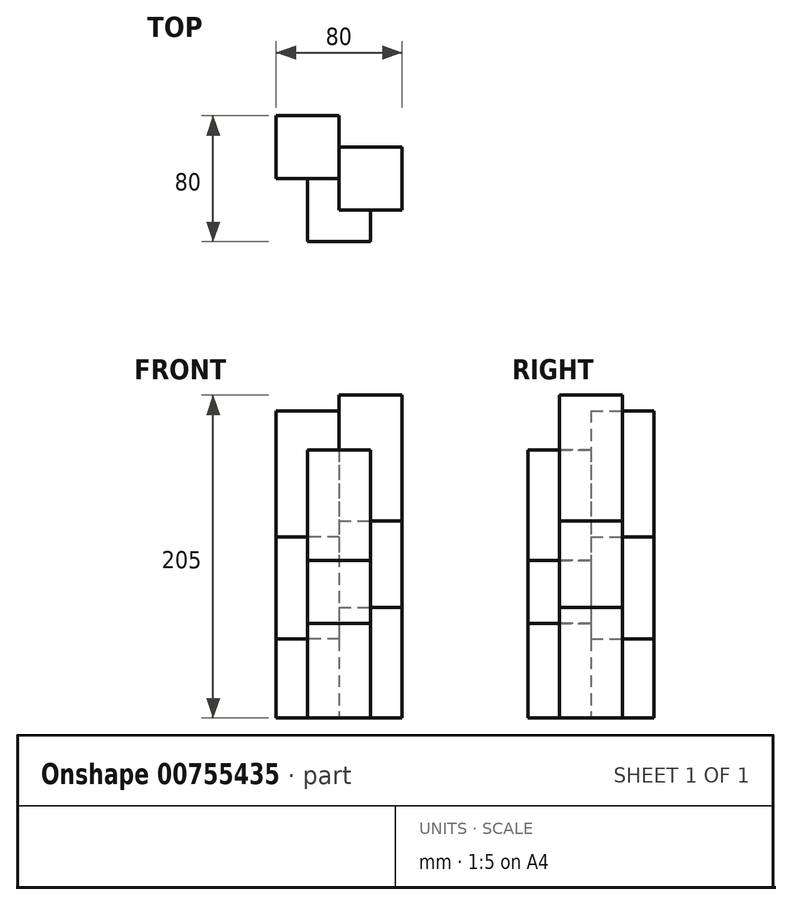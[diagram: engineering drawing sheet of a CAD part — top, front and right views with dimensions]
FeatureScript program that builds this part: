
annotation { "Feature Type Name" : "Feature", "Feature Type Description" : "" }
export const myFeature = defineFeature(function(context is Context, id is Id, definition is map)
    precondition{}
    {
        {
            var Q0;
            Q0=qCreatedBy(makeId("Top.planeOp"),FACE);
            var sketch = newSketch(context, id + "F0", { "sketchPlane" : qUnion([Q0])});
            skLineSegment(sketch, "E0.bottom", {"start": v(0, 0) * mm, "end": v(-40, 0) * mm});
            skLineSegment(sketch, "E0.top", {"start": v(0, 40) * mm, "end": v(-40, 40) * mm});
            skLineSegment(sketch, "E0.left", {"start": v(0, 0) * mm, "end": v(0, 40) * mm});
            skLineSegment(sketch, "E0.right", {"start": v(-40, 0) * mm, "end": v(-40, 40) * mm});
            skSolve(sketch);
        }
        {
            var Q0;
            Q0=makeQuery(id+"F0.imprint","IMPRINT",FACE,{"disambiguationData":[TD([[makeQuery(id+"F0.imprint","IMPRINT",EDGE,{"derivedFrom":sQuery(id+"F0.wireOp",EDGE,"E0.bottom")}),-1.0]])]});
            extrude(context, id + "F1", {"entities" : qUnion([Q0]), "depth" : 50 * mm, "offsetDistance" : 25 * mm});
        }
        {
            var Q0;
            Q0=qCreatedBy(makeId("Top.planeOp"),FACE);
            var sketch = newSketch(context, id + "F2", { "sketchPlane" : qUnion([Q0])});
            skLineSegment(sketch, "E1.bottom", {"start": v(-20, 0) * mm, "end": v(20, 0) * mm});
            skLineSegment(sketch, "E1.top", {"start": v(-20, -40) * mm, "end": v(20, -40) * mm});
            skLineSegment(sketch, "E1.left", {"start": v(-20, 0) * mm, "end": v(-20, -40) * mm});
            skLineSegment(sketch, "E1.right", {"start": v(20, 0) * mm, "end": v(20, -40) * mm});
            skSolve(sketch);
        }
        {
            var Q0;
            Q0 = qSketchRegion(id + "F2", true);
            extrude(context, id + "F3", {"entities" : qUnion([Q0]), "operationType" : NewBodyOperationType.ADD, "depth" : 60 * mm, "offsetDistance" : 25 * mm});
        }
        {
            var Q0;
            Q0=qCreatedBy(makeId("Top.planeOp"),FACE);
            var sketch = newSketch(context, id + "F4", { "sketchPlane" : qUnion([Q0])});
            skLineSegment(sketch, "E2.bottom", {"start": v(0, 20) * mm, "end": v(40, 20) * mm});
            skLineSegment(sketch, "E2.top", {"start": v(0, -20) * mm, "end": v(40, -20) * mm});
            skLineSegment(sketch, "E2.left", {"start": v(0, 20) * mm, "end": v(0, -20) * mm});
            skLineSegment(sketch, "E2.right", {"start": v(40, 20) * mm, "end": v(40, -20) * mm});
            skSolve(sketch);
        }
        {
            var Q0;
            Q0 = qSketchRegion(id + "F4", true);
            extrude(context, id + "F5", {"entities" : qUnion([Q0]), "operationType" : NewBodyOperationType.ADD, "depth" : 70 * mm, "offsetDistance" : 25 * mm});
        }
        {
            var Q0;
            Q0=makeQuery(id+"F1.opExtrude","CAP_FACE",FACE,{"disambiguationData":[OSD([sQuery(id+"F0.wireOp",EDGE,"E0.bottom"),sQuery(id+"F0.wireOp",EDGE,"E0.top"),sQuery(id+"F0.wireOp",EDGE,"E0.left"),sQuery(id+"F0.wireOp",EDGE,"E0.right")])],"isStart":false});
            var sketch = newSketch(context, id + "F6", { "sketchPlane" : qUnion([Q0])});
            skLineSegment(sketch, "E3.0.0", {"start": v(0, 0) * mm, "end": v(0, 20) * mm});
            skLineSegment(sketch, "E3.0.1", {"start": v(0, 20) * mm, "end": v(0, 40) * mm});
            skLineSegment(sketch, "E3.0.2", {"start": v(0, 40) * mm, "end": v(-40, 40) * mm});
            skLineSegment(sketch, "E3.0.3", {"start": v(-40, 40) * mm, "end": v(-40, 0) * mm});
            skLineSegment(sketch, "E3.0.4", {"start": v(-40, 0) * mm, "end": v(-20, 0) * mm});
            skLineSegment(sketch, "E3.0.5", {"start": v(-20, 0) * mm, "end": v(0, 0) * mm});
            skSolve(sketch);
        }
        {
            var Q0;
            Q0 = qSketchRegion(id + "F6", true);
            extrude(context, id + "F7", {"entities" : qUnion([Q0]), "depth" : 65 * mm, "offsetDistance" : 25 * mm});
        }
        {
            var Q0;
            Q0=makeQuery(id+"F3.opExtrude","CAP_FACE",FACE,{"disambiguationData":[OSD([sQuery(id+"F2.wireOp",EDGE,"E1.bottom"),sQuery(id+"F2.wireOp",EDGE,"E1.top"),sQuery(id+"F2.wireOp",EDGE,"E1.left"),sQuery(id+"F2.wireOp",EDGE,"E1.right")])],"isStart":false});
            var sketch = newSketch(context, id + "F8", { "sketchPlane" : qUnion([Q0])});
            skLineSegment(sketch, "E4.0.0", {"start": v(20, -20) * mm, "end": v(0, -20) * mm});
            skLineSegment(sketch, "E4.0.1", {"start": v(0, -20) * mm, "end": v(0, 0) * mm});
            skLineSegment(sketch, "E4.0.2", {"start": v(0, 0) * mm, "end": v(-20, 0) * mm});
            skLineSegment(sketch, "E4.0.3", {"start": v(-20, 0) * mm, "end": v(-20, -40) * mm});
            skLineSegment(sketch, "E4.0.4", {"start": v(-20, -40) * mm, "end": v(20, -40) * mm});
            skLineSegment(sketch, "E4.0.5", {"start": v(20, -40) * mm, "end": v(20, -20) * mm});
            skSolve(sketch);
        }
        {
            var Q0;
            Q0 = qSketchRegion(id + "F8", true);
            extrude(context, id + "F9", {"entities" : qUnion([Q0]), "depth" : 40 * mm, "offsetDistance" : 25 * mm});
        }
        {
            var Q0;
            Q0=makeQuery(id+"F5.opExtrude","CAP_FACE",FACE,{"disambiguationData":[OSD([sQuery(id+"F4.wireOp",EDGE,"E2.bottom"),sQuery(id+"F4.wireOp",EDGE,"E2.top"),sQuery(id+"F4.wireOp",EDGE,"E2.left"),sQuery(id+"F4.wireOp",EDGE,"E2.right")])],"isStart":false});
            var sketch = newSketch(context, id + "F10", { "sketchPlane" : qUnion([Q0])});
            skLineSegment(sketch, "E5.0.0", {"start": v(0, 20) * mm, "end": v(0, -20) * mm});
            skLineSegment(sketch, "E5.0.1", {"start": v(0, -20) * mm, "end": v(40, -20) * mm});
            skLineSegment(sketch, "E5.0.2", {"start": v(40, -20) * mm, "end": v(40, 20) * mm});
            skLineSegment(sketch, "E5.0.3", {"start": v(40, 20) * mm, "end": v(0, 20) * mm});
            skSolve(sketch);
        }
        {
            var Q0;
            Q0 = qSketchRegion(id + "F10", true);
            extrude(context, id + "F11", {"entities" : qUnion([Q0]), "depth" : 55 * mm, "offsetDistance" : 25 * mm});
        }
        {
            var Q0;
            Q0=makeQuery(id+"F7.opExtrude","SWEPT_BODY",BODY,{"disambiguationData":[OSD([sQuery(id+"F6.wireOp",EDGE,"E3.0.0"),sQuery(id+"F6.wireOp",EDGE,"E3.0.1"),sQuery(id+"F6.wireOp",EDGE,"E3.0.2"),sQuery(id+"F6.wireOp",EDGE,"E3.0.3"),sQuery(id+"F6.wireOp",EDGE,"E3.0.4"),sQuery(id+"F6.wireOp",EDGE,"E3.0.5")])]});
            var Q1;
            Q1=makeQuery(id+"F9.opExtrude","SWEPT_BODY",BODY,{"disambiguationData":[OSD([sQuery(id+"F8.wireOp",EDGE,"E4.0.0"),sQuery(id+"F8.wireOp",EDGE,"E4.0.1"),sQuery(id+"F8.wireOp",EDGE,"E4.0.2"),sQuery(id+"F8.wireOp",EDGE,"E4.0.3"),sQuery(id+"F8.wireOp",EDGE,"E4.0.4"),sQuery(id+"F8.wireOp",EDGE,"E4.0.5")])]});
            var Q2;
            Q2=makeQuery(id+"F11.opExtrude","SWEPT_BODY",BODY,{"disambiguationData":[OSD([sQuery(id+"F10.wireOp",EDGE,"E5.0.0"),sQuery(id+"F10.wireOp",EDGE,"E5.0.1"),sQuery(id+"F10.wireOp",EDGE,"E5.0.2"),sQuery(id+"F10.wireOp",EDGE,"E5.0.3")])]});
            booleanBodies(context, id + "F12", {"operationType" : BooleanOperationType.UNION, "tools" : qUnion([Q0, Q1, Q2])});
        }
        {
            var Q0;
            Q0=makeQuery(id+"F9.opExtrude","CAP_FACE",FACE,{"disambiguationData":[OSD([sQuery(id+"F8.wireOp",EDGE,"E4.0.0"),sQuery(id+"F8.wireOp",EDGE,"E4.0.1"),sQuery(id+"F8.wireOp",EDGE,"E4.0.2"),sQuery(id+"F8.wireOp",EDGE,"E4.0.3"),sQuery(id+"F8.wireOp",EDGE,"E4.0.4"),sQuery(id+"F8.wireOp",EDGE,"E4.0.5")])],"isStart":false});
            var sketch = newSketch(context, id + "F13", { "sketchPlane" : qUnion([Q0])});
            skLineSegment(sketch, "E6.0.0", {"start": v(20, -40) * mm, "end": v(20, -20) * mm});
            skLineSegment(sketch, "E6.0.1", {"start": v(20, -20) * mm, "end": v(0, -20) * mm});
            skLineSegment(sketch, "E6.0.2", {"start": v(0, -20) * mm, "end": v(0, 0) * mm});
            skLineSegment(sketch, "E6.0.3", {"start": v(0, 0) * mm, "end": v(-20, 0) * mm});
            skLineSegment(sketch, "E6.0.4", {"start": v(-20, 0) * mm, "end": v(-20, -40) * mm});
            skLineSegment(sketch, "E6.0.5", {"start": v(-20, -40) * mm, "end": v(20, -40) * mm});
            skSolve(sketch);
        }
        {
            var Q0;
            Q0 = qSketchRegion(id + "F13", true);
            extrude(context, id + "F14", {"entities" : qUnion([Q0]), "depth" : 70 * mm, "offsetDistance" : 25 * mm});
        }
        {
            var Q0;
            Q0=makeQuery(id+"F7.opExtrude","CAP_FACE",FACE,{"disambiguationData":[OSD([sQuery(id+"F6.wireOp",EDGE,"E3.0.0"),sQuery(id+"F6.wireOp",EDGE,"E3.0.1"),sQuery(id+"F6.wireOp",EDGE,"E3.0.2"),sQuery(id+"F6.wireOp",EDGE,"E3.0.3"),sQuery(id+"F6.wireOp",EDGE,"E3.0.4"),sQuery(id+"F6.wireOp",EDGE,"E3.0.5")])],"isStart":false});
            var sketch = newSketch(context, id + "F15", { "sketchPlane" : qUnion([Q0])});
            skLineSegment(sketch, "E7.0.0", {"start": v(-40, 0) * mm, "end": v(0, 0) * mm});
            skLineSegment(sketch, "E7.0.1", {"start": v(0, 0) * mm, "end": v(0, 20) * mm});
            skLineSegment(sketch, "E7.0.2", {"start": v(0, 20) * mm, "end": v(0, 40) * mm});
            skLineSegment(sketch, "E7.0.3", {"start": v(0, 40) * mm, "end": v(-40, 40) * mm});
            skLineSegment(sketch, "E7.0.4", {"start": v(-40, 40) * mm, "end": v(-40, 0) * mm});
            skSolve(sketch);
        }
        {
            var Q0;
            Q0 = qSketchRegion(id + "F15", true);
            extrude(context, id + "F16", {"entities" : qUnion([Q0]), "depth" : 80 * mm, "offsetDistance" : 25 * mm});
        }
        {
            var Q0;
            Q0=makeQuery(id+"F11.opExtrude","CAP_FACE",FACE,{"disambiguationData":[OSD([sQuery(id+"F10.wireOp",EDGE,"E5.0.0"),sQuery(id+"F10.wireOp",EDGE,"E5.0.1"),sQuery(id+"F10.wireOp",EDGE,"E5.0.2"),sQuery(id+"F10.wireOp",EDGE,"E5.0.3")])],"isStart":false});
            var sketch = newSketch(context, id + "F17", { "sketchPlane" : qUnion([Q0])});
            skLineSegment(sketch, "E8.0.0", {"start": v(40, 20) * mm, "end": v(0, 20) * mm});
            skLineSegment(sketch, "E8.0.1", {"start": v(0, 20) * mm, "end": v(0, -20) * mm});
            skLineSegment(sketch, "E8.0.2", {"start": v(0, -20) * mm, "end": v(40, -20) * mm});
            skLineSegment(sketch, "E8.0.3", {"start": v(40, -20) * mm, "end": v(40, 20) * mm});
            skSolve(sketch);
        }
        {
            var Q0;
            Q0 = qSketchRegion(id + "F17", true);
            extrude(context, id + "F18", {"entities" : qUnion([Q0]), "depth" : 80 * mm, "offsetDistance" : 25 * mm});
        }
    });
